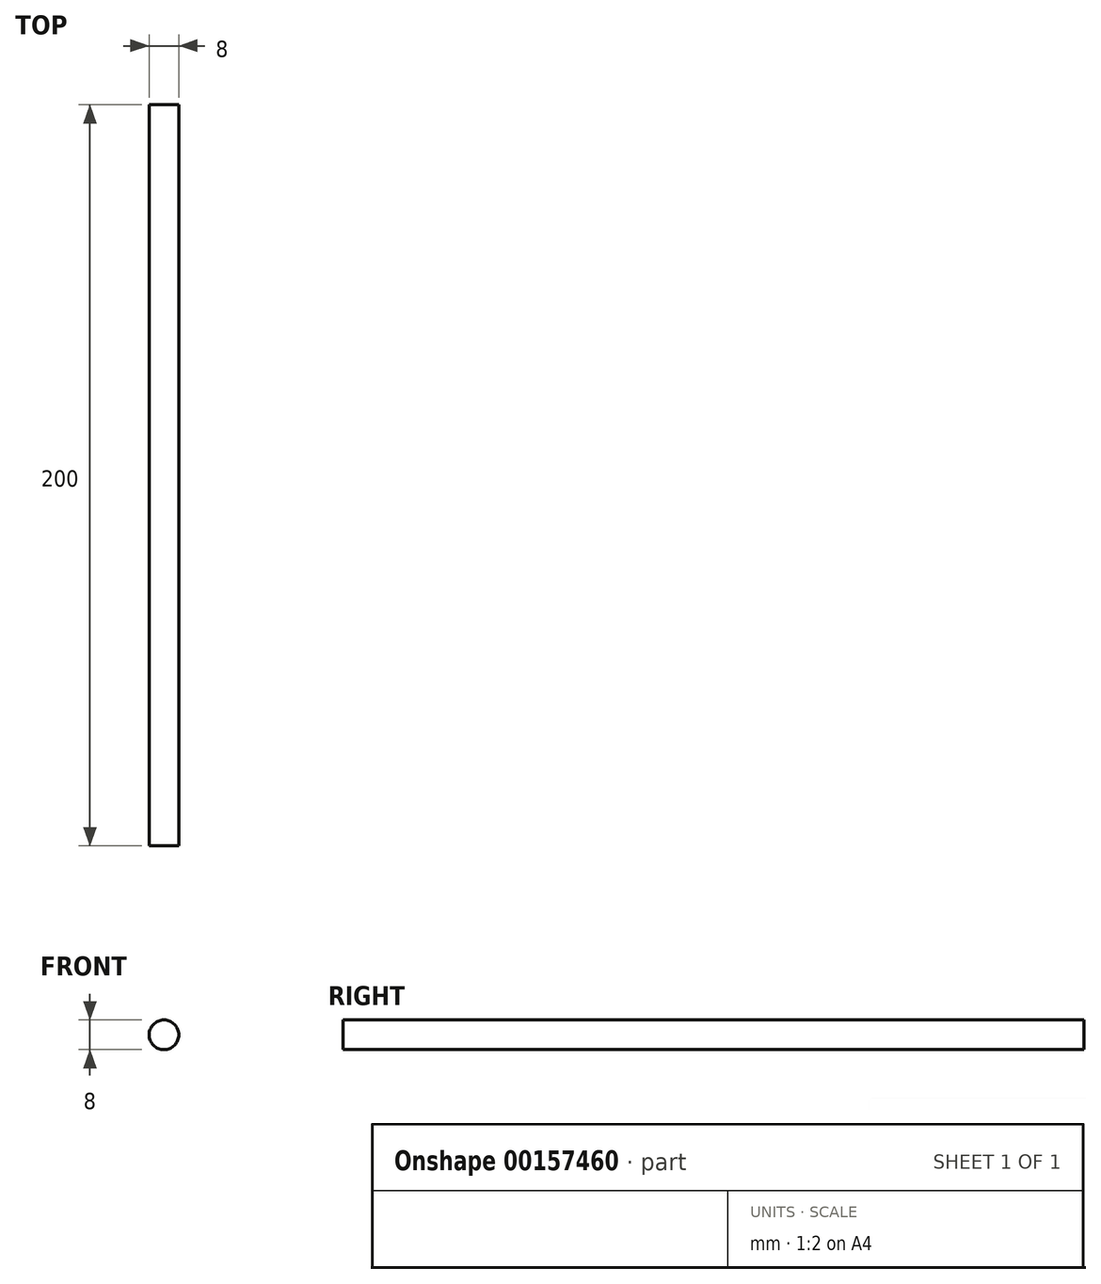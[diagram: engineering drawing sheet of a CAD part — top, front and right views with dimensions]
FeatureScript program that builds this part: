
annotation { "Feature Type Name" : "Feature", "Feature Type Description" : "" }
export const myFeature = defineFeature(function(context is Context, id is Id, definition is map)
    precondition{}
    {
        {
            var Q0;
            Q0=qCreatedBy(makeId("Front.planeOp"),FACE);
            var sketch = newSketch(context, id + "F0", { "sketchPlane" : qUnion([Q0])});
            skCircle(sketch, "E0", {"center": v(0, 0) * mm, "radius": 4 * mm});
            skSolve(sketch);
        }
        {
            var Q0;
            Q0=makeQuery(id+"F0.imprint","IMPRINT",FACE,{"disambiguationData":[TD([[makeQuery(id+"F0.imprint","IMPRINT",EDGE,{"derivedFrom":sQuery(id+"F0.wireOp",EDGE,"E0")}),1.0]])]});
            extrude(context, id + "F1", {"entities" : qUnion([Q0]), "depth" : 200 * mm});
        }
    });
